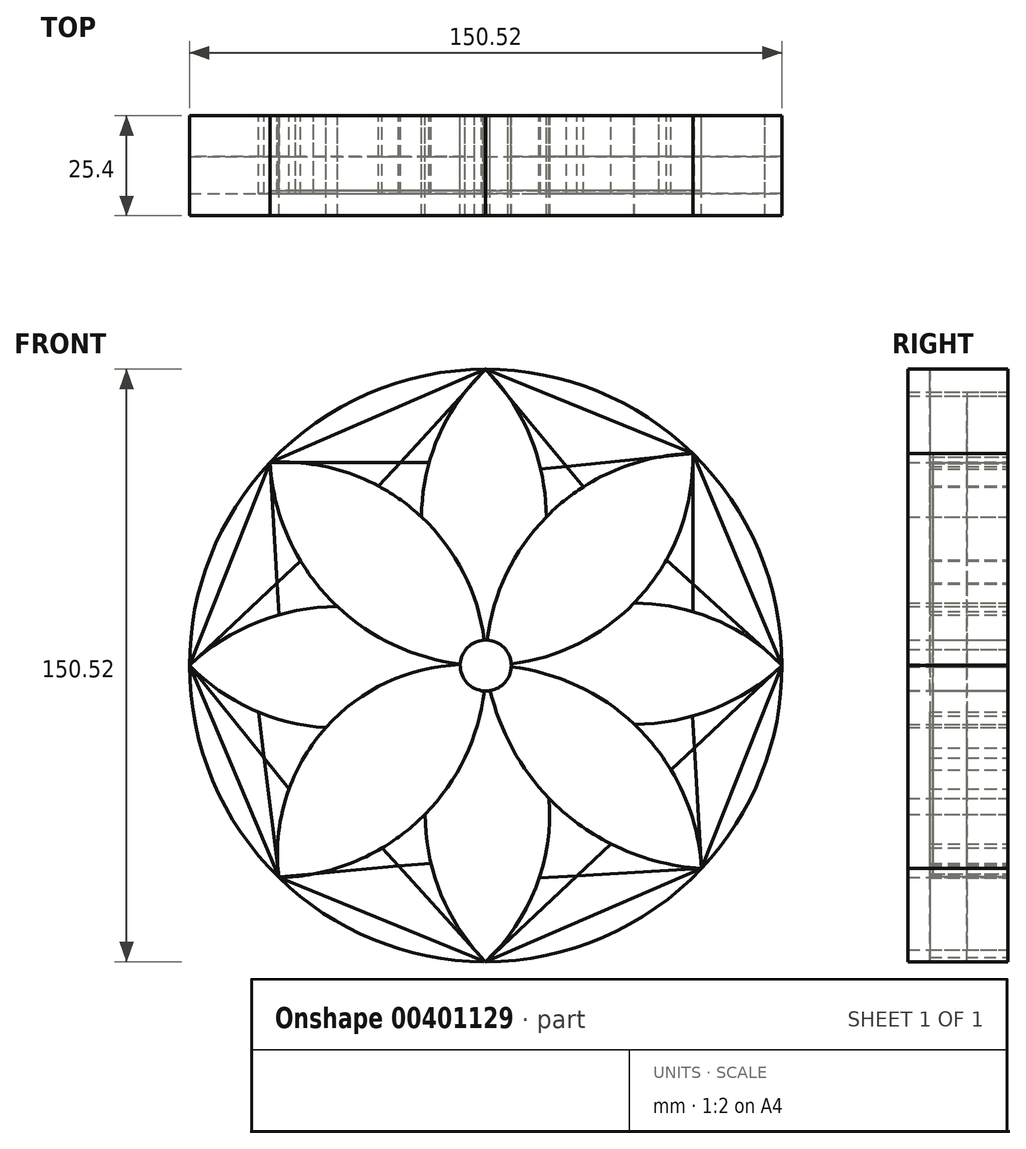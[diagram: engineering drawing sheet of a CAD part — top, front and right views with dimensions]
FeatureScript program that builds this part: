
annotation { "Feature Type Name" : "Feature", "Feature Type Description" : "" }
export const myFeature = defineFeature(function(context is Context, id is Id, definition is map)
    precondition{}
    {
        {
            var Q0;
            Q0=qCreatedBy(makeId("Front.planeOp"),FACE);
            var sketch = newSketch(context, id + "F0", { "sketchPlane" : qUnion([Q0])});
            skCircle(sketch, "E0", {"center": v(0, 0) * mm, "radius": 75.26 * mm});
            skCircle(sketch, "E1", {"center": v(0, 0) * mm, "radius": 6.49 * mm});
            skArc(sketch, "E2", {"start": v(0, 75.26) * mm, "mid": v(-12.03, 58.18) * mm, "end": v(-16.3, 37.72) * mm});
            skArc(sketch, "E3", {"start": v(15.38, 37.73) * mm, "mid": v(11.37, 58) * mm, "end": v(0, 75.26) * mm});
            skArc(sketch, "E4", {"start": v(75.26, 0) * mm, "mid": v(58.07, 11.72) * mm, "end": v(37.68, 15.86) * mm});
            skArc(sketch, "E5", {"start": v(37.72, -14.94) * mm, "mid": v(57.92, -11.05) * mm, "end": v(75.26, 0) * mm});
            skArc(sketch, "E6", {"start": v(-0.06, -75.26) * mm, "mid": v(12.73, -56.35) * mm, "end": v(16.12, -33.78) * mm});
            skArc(sketch, "E7", {"start": v(-15.42, -37.83) * mm, "mid": v(-15.03, -44.13) * mm, "end": v(-13.9, -50.35) * mm});
            skArc(sketch, "E8", {"start": v(-75.26, 0) * mm, "mid": v(-59.41, -11.13) * mm, "end": v(-40.6, -15.77) * mm});
            skArc(sketch, "E9", {"start": v(52.61, 53.82) * mm, "mid": v(17.65, 39.9) * mm, "end": v(0.38, 6.47) * mm});
            skArc(sketch, "E10", {"start": v(54.83, -51.55) * mm, "mid": v(39.96, -17.17) * mm, "end": v(6.47, -0.37) * mm});
            skArc(sketch, "E11", {"start": v(1.14, -6.38) * mm, "mid": v(20.5, -37.86) * mm, "end": v(54.83, -51.55) * mm});
            skArc(sketch, "E12", {"start": v(-52.56, -53.87) * mm, "mid": v(-17.6, -39.93) * mm, "end": v(-0.37, -6.47) * mm});
            skArc(sketch, "E13", {"start": v(-6.48, 0.2) * mm, "mid": v(-41.42, -16.7) * mm, "end": v(-52.56, -53.87) * mm});
            skArc(sketch, "E14", {"start": v(-54.83, 51.55) * mm, "mid": v(-39.94, 17.2) * mm, "end": v(-6.47, 0.38) * mm});
            skLineSegment(sketch, "E15", {"start": v(-0.1, 0.1) * mm, "end": v(-0.1, 0.1) * mm});
            skLineSegment(sketch, "E16.trimOffspring", {"start": v(0, 0) * mm, "end": v(0, 0) * mm});
            skArc(sketch, "E17.trimOffspring", {"start": v(6.47, 0.4) * mm, "mid": v(39.84, 18.21) * mm, "end": v(52.61, 53.82) * mm});
            skArc(sketch, "E18.trimOffspring", {"start": v(-37.68, 14.94) * mm, "mid": v(-57.9, 11.06) * mm, "end": v(-75.26, 0) * mm});
            skArc(sketch, "E19.trimOffspring", {"start": v(-0.4, 6.47) * mm, "mid": v(-18.67, 39.81) * mm, "end": v(-54.83, 51.55) * mm});
            skLineSegment(sketch, "E20", {"start": v(-75.26, 0) * mm, "end": v(-54.83, 51.55) * mm});
            skLineSegment(sketch, "E21", {"start": v(-54.83, 51.55) * mm, "end": v(-52.47, 12.9) * mm});
            skLineSegment(sketch, "E22", {"start": v(-75.26, 0) * mm, "end": v(-47.06, 26.58) * mm});
            skLineSegment(sketch, "E23", {"start": v(52.61, 53.82) * mm, "end": v(75.26, 0) * mm});
            skLineSegment(sketch, "E24", {"start": v(75.26, 0) * mm, "end": v(45.9, 26.86) * mm});
            skPoint(sketch, "E25.endSnap0", {"position": v(49.26, 40.34) * mm});
            skPoint(sketch, "E25.end.orphan", {"position": v(49.26, 14.55) * mm});
            skLineSegment(sketch, "E26", {"start": v(52.61, 53.82) * mm, "end": v(52.61, 13.68) * mm});
            skLineSegment(sketch, "E27", {"start": v(-75.26, 0) * mm, "end": v(-52.56, -53.87) * mm});
            skLineSegment(sketch, "E28", {"start": v(-52.56, -53.87) * mm, "end": v(-57.77, -11.84) * mm});
            skLineSegment(sketch, "E29", {"start": v(-75.26, 0) * mm, "end": v(-49.97, -31.35) * mm});
            skLineSegment(sketch, "E30", {"start": v(75.26, 0) * mm, "end": v(54.83, -51.55) * mm});
            skLineSegment(sketch, "E31", {"start": v(54.83, -51.55) * mm, "end": v(52.52, -12.88) * mm});
            skLineSegment(sketch, "E32", {"start": v(75.26, 0) * mm, "end": v(47.08, -26.56) * mm});
            skLineSegment(sketch, "E33", {"start": v(-54.83, 51.55) * mm, "end": v(0, 75.26) * mm});
            skLineSegment(sketch, "E34", {"start": v(0, 75.26) * mm, "end": v(-27.21, 45.55) * mm});
            skLineSegment(sketch, "E35", {"start": v(-54.83, 51.55) * mm, "end": v(-14.39, 51.55) * mm});
            skLineSegment(sketch, "E36", {"start": v(0, 75.26) * mm, "end": v(52.61, 53.82) * mm});
            skLineSegment(sketch, "E37", {"start": v(52.61, 53.82) * mm, "end": v(13.97, 49.86) * mm});
            skLineSegment(sketch, "E38", {"start": v(0, 75.26) * mm, "end": v(24.84, 45.4) * mm});
            skLineSegment(sketch, "E39", {"start": v(-52.56, -53.87) * mm, "end": v(-0.06, -75.26) * mm});
            skLineSegment(sketch, "E40", {"start": v(-52.57, -53.76) * mm, "end": v(-52.59, -53.77) * mm});
            skLineSegment(sketch, "E41", {"start": v(-52.59, -53.77) * mm, "end": v(-13.97, -50.22) * mm});
            skLineSegment(sketch, "E42", {"start": v(-13.97, -50.22) * mm, "end": v(-13.9, -50.35) * mm});
            skArc(sketch, "E43.trimOffspring", {"start": v(-1.12, -74.14) * mm, "mid": v(-0.6, -74.7) * mm, "end": v(-0.06, -75.26) * mm});
            skLineSegment(sketch, "E44", {"start": v(-26.3, -46.36) * mm, "end": v(-0.06, -75.26) * mm});
            skLineSegment(sketch, "E45", {"start": v(-0.06, -75.26) * mm, "end": v(54.83, -51.55) * mm});
            skLineSegment(sketch, "E46", {"start": v(54.83, -51.55) * mm, "end": v(13.58, -54.02) * mm});
            skLineSegment(sketch, "E47", {"start": v(-0.2, -75.11) * mm, "end": v(-0.42, -75.46) * mm});
            skLineSegment(sketch, "E48", {"start": v(-0.06, -75.26) * mm, "end": v(31.85, -45.35) * mm});
            skArc(sketch, "E49", {"start": v(-15.42, -37.83) * mm, "mid": v(-11.4, -58.05) * mm, "end": v(-0.06, -75.26) * mm});
            skLineSegment(sketch, "E50.trimOffspring", {"start": v(-1.2, -74) * mm, "end": v(-0.42, -75.46) * mm});
            skSolve(sketch);
        }
        {
            var Q0;
            {var subQ0=sQuery(id+"F0.wireOp",EDGE,"E20");Q0=makeQuery(id+"F0.imprint","IMPRINT",FACE,{"disambiguationData":[TD([[makeQuery(id+"F0.imprint","IMPRINT",EDGE,{"derivedFrom":subQ0}),1.0]])]});}
            var Q1;
            {var subQ0=sQuery(id+"F0.wireOp",EDGE,"E33");Q1=makeQuery(id+"F0.imprint","IMPRINT",FACE,{"disambiguationData":[TD([[makeQuery(id+"F0.imprint","IMPRINT",EDGE,{"derivedFrom":subQ0}),1.0]])]});}
            var Q2;
            {var subQ0=sQuery(id+"F0.wireOp",EDGE,"E36");Q2=makeQuery(id+"F0.imprint","IMPRINT",FACE,{"disambiguationData":[TD([[makeQuery(id+"F0.imprint","IMPRINT",EDGE,{"derivedFrom":subQ0}),1.0]])]});}
            var Q3;
            {var subQ0=sQuery(id+"F0.wireOp",EDGE,"E23");Q3=makeQuery(id+"F0.imprint","IMPRINT",FACE,{"disambiguationData":[TD([[makeQuery(id+"F0.imprint","IMPRINT",EDGE,{"derivedFrom":subQ0}),1.0]])]});}
            var Q4;
            {var subQ0=sQuery(id+"F0.wireOp",EDGE,"E30");Q4=makeQuery(id+"F0.imprint","IMPRINT",FACE,{"disambiguationData":[TD([[makeQuery(id+"F0.imprint","IMPRINT",EDGE,{"derivedFrom":subQ0}),1.0]])]});}
            var Q5;
            {var subQ0=sQuery(id+"F0.wireOp",EDGE,"E45");Q5=makeQuery(id+"F0.imprint","IMPRINT",FACE,{"disambiguationData":[TD([[makeQuery(id+"F0.imprint","IMPRINT",EDGE,{"derivedFrom":subQ0}),-1.0]])]});}
            var Q6;
            {var subQ1=sQuery(id+"F0.wireOp",EDGE,"E0");var subQ3=sQuery(id+"F0.wireOp",EDGE,"E50.trimOffspring");var subQ4=makeQuery(id+"F0.imprint","INTERSECT",VERTEX,{"derivedFrom":[subQ1,subQ3]});Q6=makeQuery(id+"F0.imprint","IMPRINT",FACE,{"disambiguationData":[TD([[makeQuery(id+"F0.imprint","IMPRINT",EDGE,{"disambiguationData":[TD([[subQ4,1.0]])],"derivedFrom":subQ3}),-1.0]])]});}
            var Q7;
            {var subQ0=sQuery(id+"F0.wireOp",EDGE,"E27");Q7=makeQuery(id+"F0.imprint","IMPRINT",FACE,{"disambiguationData":[TD([[makeQuery(id+"F0.imprint","IMPRINT",EDGE,{"derivedFrom":subQ0}),-1.0]])]});}
            var Q8;
            {var subQ0=sQuery(id+"F0.wireOp",EDGE,"E13");var subQ3=sQuery(id+"F0.wireOp",EDGE,"E1");var subQ4=makeQuery(id+"F0.imprint","INTERSECT",VERTEX,{"derivedFrom":[subQ3,subQ0]});Q8=makeQuery(id+"F0.imprint","IMPRINT",FACE,{"disambiguationData":[TD([[makeQuery(id+"F0.imprint","IMPRINT",EDGE,{"disambiguationData":[TD([[subQ4,1.0]])],"derivedFrom":subQ3}),-1.0]])]});}
            var Q9;
            {var subQ8=sQuery(id+"F0.wireOp",EDGE,"E10");var subQ11=sQuery(id+"F0.wireOp",EDGE,"E1");var subQ12=makeQuery(id+"F0.imprint","INTERSECT",VERTEX,{"derivedFrom":[subQ11,subQ8]});Q9=makeQuery(id+"F0.imprint","IMPRINT",FACE,{"disambiguationData":[TD([[makeQuery(id+"F0.imprint","IMPRINT",EDGE,{"disambiguationData":[TD([[subQ12,-1.0]])],"derivedFrom":subQ11}),-1.0]])]});}
            var Q10;
            {var subQ6=sQuery(id+"F0.wireOp",EDGE,"E9");var subQ10=sQuery(id+"F0.wireOp",EDGE,"E1");var subQ11=makeQuery(id+"F0.imprint","INTERSECT",VERTEX,{"derivedFrom":[subQ10,subQ6]});Q10=makeQuery(id+"F0.imprint","IMPRINT",FACE,{"disambiguationData":[TD([[makeQuery(id+"F0.imprint","IMPRINT",EDGE,{"disambiguationData":[TD([[subQ11,-1.0]])],"derivedFrom":subQ10}),-1.0]])]});}
            var Q11;
            {var subQ5=sQuery(id+"F0.wireOp",EDGE,"E11");var subQ7=sQuery(id+"F0.wireOp",EDGE,"E1");var subQ8=makeQuery(id+"F0.imprint","INTERSECT",VERTEX,{"derivedFrom":[subQ7,subQ5]});Q11=makeQuery(id+"F0.imprint","IMPRINT",FACE,{"disambiguationData":[TD([[makeQuery(id+"F0.imprint","IMPRINT",EDGE,{"disambiguationData":[TD([[subQ8,1.0]])],"derivedFrom":subQ7}),-1.0]])]});}
            extrude(context, id + "F1", {"entities" : qUnion([Q0, Q1, Q2, Q3, Q4, Q5, Q6, Q7, Q8, Q9, Q10, Q11]), "depth" : 25.4 * mm});
        }
        {
            var Q0;
            {var subQ0=sQuery(id+"F0.wireOp",EDGE,"E9");var subQ2=sQuery(id+"F0.wireOp",EDGE,"E1");var subQ3=makeQuery(id+"F0.imprint","INTERSECT",VERTEX,{"derivedFrom":[subQ2,subQ0]});Q0=makeQuery(id+"F0.imprint","IMPRINT",FACE,{"disambiguationData":[TD([[makeQuery(id+"F0.imprint","IMPRINT",EDGE,{"disambiguationData":[TD([[subQ3,1.0]])],"derivedFrom":subQ2}),-1.0]])]});}
            var Q1;
            {var subQ0=sQuery(id+"F0.wireOp",EDGE,"E10");var subQ2=sQuery(id+"F0.wireOp",EDGE,"E1");var subQ3=makeQuery(id+"F0.imprint","INTERSECT",VERTEX,{"derivedFrom":[subQ2,subQ0]});Q1=makeQuery(id+"F0.imprint","IMPRINT",FACE,{"disambiguationData":[TD([[makeQuery(id+"F0.imprint","IMPRINT",EDGE,{"disambiguationData":[TD([[subQ3,1.0]])],"derivedFrom":subQ2}),-1.0]])]});}
            var Q2;
            {var subQ0=sQuery(id+"F0.wireOp",EDGE,"E12");var subQ1=sQuery(id+"F0.wireOp",EDGE,"E1");var subQ2=makeQuery(id+"F0.imprint","INTERSECT",VERTEX,{"derivedFrom":[subQ1,subQ0]});Q2=makeQuery(id+"F0.imprint","IMPRINT",FACE,{"disambiguationData":[TD([[makeQuery(id+"F0.imprint","IMPRINT",EDGE,{"disambiguationData":[TD([[subQ2,1.0]])],"derivedFrom":subQ1}),-1.0]])]});}
            var Q3;
            {var subQ0=sQuery(id+"F0.wireOp",EDGE,"E14");var subQ1=sQuery(id+"F0.wireOp",EDGE,"E1");var subQ2=makeQuery(id+"F0.imprint","INTERSECT",VERTEX,{"derivedFrom":[subQ1,subQ0]});Q3=makeQuery(id+"F0.imprint","IMPRINT",FACE,{"disambiguationData":[TD([[makeQuery(id+"F0.imprint","IMPRINT",EDGE,{"disambiguationData":[TD([[subQ2,1.0]])],"derivedFrom":subQ1}),-1.0]])]});}
            extrude(context, id + "F2", {"entities" : qUnion([Q0, Q1, Q2, Q3]), "depth" : 19.05 * mm});
        }
        {
            var Q0;
            {var subQ0=sQuery(id+"F0.wireOp",EDGE,"E1");var subQ4=makeQuery(id+"F0.imprint","INTERSECT",VERTEX,{"derivedFrom":[subQ0,sQuery(id+"F0.wireOp",EDGE,"E9")]});Q0=makeQuery(id+"F0.imprint","IMPRINT",FACE,{"disambiguationData":[TD([[makeQuery(id+"F0.imprint","IMPRINT",EDGE,{"disambiguationData":[TD([[subQ4,1.0]])],"derivedFrom":subQ0}),1.0]])]});}
            var Q1;
            {var subQ0=sQuery(id+"F0.wireOp",EDGE,"E20");Q1=makeQuery(id+"F0.imprint","IMPRINT",FACE,{"disambiguationData":[TD([[makeQuery(id+"F0.imprint","IMPRINT",EDGE,{"derivedFrom":subQ0}),-1.0]])]});}
            var Q2;
            {var subQ5=sQuery(id+"F0.wireOp",EDGE,"E33");Q2=makeQuery(id+"F0.imprint","IMPRINT",FACE,{"disambiguationData":[TD([[makeQuery(id+"F0.imprint","IMPRINT",EDGE,{"derivedFrom":subQ5}),-1.0]])]});}
            var Q3;
            {var subQ5=sQuery(id+"F0.wireOp",EDGE,"E36");Q3=makeQuery(id+"F0.imprint","IMPRINT",FACE,{"disambiguationData":[TD([[makeQuery(id+"F0.imprint","IMPRINT",EDGE,{"derivedFrom":subQ5}),-1.0]])]});}
            var Q4;
            {var subQ5=sQuery(id+"F0.wireOp",EDGE,"E23");Q4=makeQuery(id+"F0.imprint","IMPRINT",FACE,{"disambiguationData":[TD([[makeQuery(id+"F0.imprint","IMPRINT",EDGE,{"derivedFrom":subQ5}),-1.0]])]});}
            var Q5;
            {var subQ0=sQuery(id+"F0.wireOp",EDGE,"E30");Q5=makeQuery(id+"F0.imprint","IMPRINT",FACE,{"disambiguationData":[TD([[makeQuery(id+"F0.imprint","IMPRINT",EDGE,{"derivedFrom":subQ0}),-1.0]])]});}
            var Q6;
            {var subQ0=sQuery(id+"F0.wireOp",EDGE,"E45");Q6=makeQuery(id+"F0.imprint","IMPRINT",FACE,{"disambiguationData":[TD([[makeQuery(id+"F0.imprint","IMPRINT",EDGE,{"derivedFrom":subQ0}),1.0]])]});}
            var Q7;
            {var subQ0=sQuery(id+"F0.wireOp",EDGE,"E41");var subQ1=sQuery(id+"F0.wireOp",EDGE,"E12");var subQ2=makeQuery(id+"F0.imprint","INTERSECT",VERTEX,{"derivedFrom":[subQ1,subQ0]});Q7=makeQuery(id+"F0.imprint","IMPRINT",FACE,{"disambiguationData":[TD([[makeQuery(id+"F0.imprint","IMPRINT",EDGE,{"disambiguationData":[TD([[subQ2,-1.0]])],"derivedFrom":subQ0}),-1.0]])]});}
            var Q8;
            {var subQ4=sQuery(id+"F0.wireOp",EDGE,"E27");Q8=makeQuery(id+"F0.imprint","IMPRINT",FACE,{"disambiguationData":[TD([[makeQuery(id+"F0.imprint","IMPRINT",EDGE,{"derivedFrom":subQ4}),1.0]])]});}
            var Q9;
            {var subQ0=sQuery(id+"F0.wireOp",EDGE,"E13");var subQ1=sQuery(id+"F0.wireOp",EDGE,"E8");var subQ2=makeQuery(id+"F0.imprint","INTERSECT",VERTEX,{"derivedFrom":[subQ1,subQ0]});Q9=makeQuery(id+"F0.imprint","IMPRINT",FACE,{"disambiguationData":[TD([[makeQuery(id+"F0.imprint","IMPRINT",EDGE,{"disambiguationData":[TD([[subQ2,1.0]])],"derivedFrom":subQ1}),-1.0]])]});}
            var Q10;
            {var subQ5=sQuery(id+"F0.wireOp",EDGE,"E42");Q10=makeQuery(id+"F0.imprint","IMPRINT",FACE,{"disambiguationData":[TD([[makeQuery(id+"F0.imprint","IMPRINT",EDGE,{"derivedFrom":subQ5}),1.0]])]});}
            var Q11;
            {var subQ0=sQuery(id+"F0.wireOp",EDGE,"E11");var subQ1=sQuery(id+"F0.wireOp",EDGE,"E6");var subQ2=makeQuery(id+"F0.imprint","INTERSECT",VERTEX,{"derivedFrom":[subQ1,subQ0]});Q11=makeQuery(id+"F0.imprint","IMPRINT",FACE,{"disambiguationData":[TD([[makeQuery(id+"F0.imprint","IMPRINT",EDGE,{"disambiguationData":[TD([[subQ2,1.0]])],"derivedFrom":subQ1}),-1.0]])]});}
            var Q12;
            {var subQ0=sQuery(id+"F0.wireOp",EDGE,"E10");var subQ1=sQuery(id+"F0.wireOp",EDGE,"E5");var subQ2=makeQuery(id+"F0.imprint","INTERSECT",VERTEX,{"derivedFrom":[subQ1,subQ0]});Q12=makeQuery(id+"F0.imprint","IMPRINT",FACE,{"disambiguationData":[TD([[makeQuery(id+"F0.imprint","IMPRINT",EDGE,{"disambiguationData":[TD([[subQ2,-1.0]])],"derivedFrom":subQ1}),-1.0]])]});}
            var Q13;
            {var subQ0=sQuery(id+"F0.wireOp",EDGE,"E17.trimOffspring");var subQ1=sQuery(id+"F0.wireOp",EDGE,"E4");var subQ2=makeQuery(id+"F0.imprint","INTERSECT",VERTEX,{"derivedFrom":[subQ1,subQ0]});Q13=makeQuery(id+"F0.imprint","IMPRINT",FACE,{"disambiguationData":[TD([[makeQuery(id+"F0.imprint","IMPRINT",EDGE,{"disambiguationData":[TD([[subQ2,1.0]])],"derivedFrom":subQ1}),-1.0]])]});}
            var Q14;
            {var subQ0=sQuery(id+"F0.wireOp",EDGE,"E9");var subQ1=sQuery(id+"F0.wireOp",EDGE,"E3");var subQ2=makeQuery(id+"F0.imprint","INTERSECT",VERTEX,{"derivedFrom":[subQ1,subQ0]});Q14=makeQuery(id+"F0.imprint","IMPRINT",FACE,{"disambiguationData":[TD([[makeQuery(id+"F0.imprint","IMPRINT",EDGE,{"disambiguationData":[TD([[subQ2,-1.0]])],"derivedFrom":subQ1}),-1.0]])]});}
            var Q15;
            {var subQ0=sQuery(id+"F0.wireOp",EDGE,"E19.trimOffspring");var subQ1=sQuery(id+"F0.wireOp",EDGE,"E2");var subQ2=makeQuery(id+"F0.imprint","INTERSECT",VERTEX,{"derivedFrom":[subQ1,subQ0]});Q15=makeQuery(id+"F0.imprint","IMPRINT",FACE,{"disambiguationData":[TD([[makeQuery(id+"F0.imprint","IMPRINT",EDGE,{"disambiguationData":[TD([[subQ2,1.0]])],"derivedFrom":subQ1}),-1.0]])]});}
            var Q16;
            {var subQ0=sQuery(id+"F0.wireOp",EDGE,"E18.trimOffspring");var subQ1=sQuery(id+"F0.wireOp",EDGE,"E14");var subQ2=makeQuery(id+"F0.imprint","INTERSECT",VERTEX,{"derivedFrom":[subQ1,subQ0]});Q16=makeQuery(id+"F0.imprint","IMPRINT",FACE,{"disambiguationData":[TD([[makeQuery(id+"F0.imprint","IMPRINT",EDGE,{"disambiguationData":[TD([[subQ2,1.0]])],"derivedFrom":subQ1}),-1.0]])]});}
            extrude(context, id + "F3", {"entities" : qUnion([Q0, Q1, Q2, Q3, Q4, Q5, Q6, Q7, Q8, Q9, Q10, Q11, Q12, Q13, Q14, Q15, Q16]), "depth" : 19.8 * mm});
        }
        {
            var Q0;
            {var subQ0=sQuery(id+"F0.wireOp",EDGE,"E37");var subQ1=sQuery(id+"F0.wireOp",EDGE,"E3");var subQ2=makeQuery(id+"F0.imprint","INTERSECT",VERTEX,{"derivedFrom":[subQ1,subQ0]});Q0=makeQuery(id+"F0.imprint","IMPRINT",FACE,{"disambiguationData":[TD([[makeQuery(id+"F0.imprint","IMPRINT",EDGE,{"disambiguationData":[TD([[subQ2,-1.0]])],"derivedFrom":subQ1}),-1.0]])]});}
            var Q1;
            {var subQ0=sQuery(id+"F0.wireOp",EDGE,"E38");var subQ1=sQuery(id+"F0.wireOp",EDGE,"E9");var subQ2=makeQuery(id+"F0.imprint","INTERSECT",VERTEX,{"derivedFrom":[subQ1,subQ0]});Q1=makeQuery(id+"F0.imprint","IMPRINT",FACE,{"disambiguationData":[TD([[makeQuery(id+"F0.imprint","IMPRINT",EDGE,{"disambiguationData":[TD([[subQ2,1.0]])],"derivedFrom":subQ1}),-1.0]])]});}
            var Q2;
            {var subQ0=sQuery(id+"F0.wireOp",EDGE,"E24");var subQ1=sQuery(id+"F0.wireOp",EDGE,"E17.trimOffspring");var subQ2=makeQuery(id+"F0.imprint","INTERSECT",VERTEX,{"derivedFrom":[subQ1,subQ0]});Q2=makeQuery(id+"F0.imprint","IMPRINT",FACE,{"disambiguationData":[TD([[makeQuery(id+"F0.imprint","IMPRINT",EDGE,{"disambiguationData":[TD([[subQ2,-1.0]])],"derivedFrom":subQ1}),-1.0]])]});}
            var Q3;
            {var subQ0=sQuery(id+"F0.wireOp",EDGE,"E26");var subQ1=sQuery(id+"F0.wireOp",EDGE,"E4");var subQ2=makeQuery(id+"F0.imprint","INTERSECT",VERTEX,{"derivedFrom":[subQ1,subQ0]});Q3=makeQuery(id+"F0.imprint","IMPRINT",FACE,{"disambiguationData":[TD([[makeQuery(id+"F0.imprint","IMPRINT",EDGE,{"disambiguationData":[TD([[subQ2,1.0]])],"derivedFrom":subQ1}),-1.0]])]});}
            var Q4;
            {var subQ1=sQuery(id+"F0.wireOp",EDGE,"E5");var subQ3=sQuery(id+"F0.wireOp",EDGE,"E31");var subQ4=makeQuery(id+"F0.imprint","INTERSECT",VERTEX,{"derivedFrom":[subQ1,subQ3]});Q4=makeQuery(id+"F0.imprint","IMPRINT",FACE,{"disambiguationData":[TD([[makeQuery(id+"F0.imprint","IMPRINT",EDGE,{"disambiguationData":[TD([[subQ4,1.0]])],"derivedFrom":subQ3}),-1.0]])]});}
            var Q5;
            {var subQ1=sQuery(id+"F0.wireOp",EDGE,"E10");var subQ3=sQuery(id+"F0.wireOp",EDGE,"E32");var subQ4=makeQuery(id+"F0.imprint","INTERSECT",VERTEX,{"derivedFrom":[subQ1,subQ3]});Q5=makeQuery(id+"F0.imprint","IMPRINT",FACE,{"disambiguationData":[TD([[makeQuery(id+"F0.imprint","IMPRINT",EDGE,{"disambiguationData":[TD([[subQ4,1.0]])],"derivedFrom":subQ3}),1.0]])]});}
            var Q6;
            {var subQ1=sQuery(id+"F0.wireOp",EDGE,"E11");var subQ3=sQuery(id+"F0.wireOp",EDGE,"E48");var subQ4=makeQuery(id+"F0.imprint","INTERSECT",VERTEX,{"derivedFrom":[subQ1,subQ3]});Q6=makeQuery(id+"F0.imprint","IMPRINT",FACE,{"disambiguationData":[TD([[makeQuery(id+"F0.imprint","IMPRINT",EDGE,{"disambiguationData":[TD([[subQ4,1.0]])],"derivedFrom":subQ3}),-1.0]])]});}
            var Q7;
            {var subQ1=sQuery(id+"F0.wireOp",EDGE,"E6");var subQ3=sQuery(id+"F0.wireOp",EDGE,"E46");var subQ4=makeQuery(id+"F0.imprint","INTERSECT",VERTEX,{"derivedFrom":[subQ1,subQ3]});Q7=makeQuery(id+"F0.imprint","IMPRINT",FACE,{"disambiguationData":[TD([[makeQuery(id+"F0.imprint","IMPRINT",EDGE,{"disambiguationData":[TD([[subQ4,1.0]])],"derivedFrom":subQ3}),1.0]])]});}
            var Q8;
            {var subQ0=sQuery(id+"F0.wireOp",EDGE,"E42");Q8=makeQuery(id+"F0.imprint","IMPRINT",FACE,{"disambiguationData":[TD([[makeQuery(id+"F0.imprint","IMPRINT",EDGE,{"derivedFrom":subQ0}),-1.0]])]});}
            var Q9;
            {var subQ0=sQuery(id+"F0.wireOp",EDGE,"E44");var subQ1=sQuery(id+"F0.wireOp",EDGE,"E12");var subQ2=makeQuery(id+"F0.imprint","INTERSECT",VERTEX,{"derivedFrom":[subQ1,subQ0]});Q9=makeQuery(id+"F0.imprint","IMPRINT",FACE,{"disambiguationData":[TD([[makeQuery(id+"F0.imprint","IMPRINT",EDGE,{"disambiguationData":[TD([[subQ2,1.0]])],"derivedFrom":subQ1}),-1.0]])]});}
            var Q10;
            {var subQ0=sQuery(id+"F0.wireOp",EDGE,"E29");var subQ1=sQuery(id+"F0.wireOp",EDGE,"E13");var subQ2=makeQuery(id+"F0.imprint","INTERSECT",VERTEX,{"derivedFrom":[subQ1,subQ0]});Q10=makeQuery(id+"F0.imprint","IMPRINT",FACE,{"disambiguationData":[TD([[makeQuery(id+"F0.imprint","IMPRINT",EDGE,{"disambiguationData":[TD([[subQ2,-1.0]])],"derivedFrom":subQ1}),-1.0]])]});}
            var Q11;
            {var subQ1=sQuery(id+"F0.wireOp",EDGE,"E8");var subQ3=sQuery(id+"F0.wireOp",EDGE,"E28");var subQ4=makeQuery(id+"F0.imprint","INTERSECT",VERTEX,{"derivedFrom":[subQ1,subQ3]});Q11=makeQuery(id+"F0.imprint","IMPRINT",FACE,{"disambiguationData":[TD([[makeQuery(id+"F0.imprint","IMPRINT",EDGE,{"disambiguationData":[TD([[subQ4,1.0]])],"derivedFrom":subQ3}),1.0]])]});}
            var Q12;
            {var subQ1=sQuery(id+"F0.wireOp",EDGE,"E18.trimOffspring");var subQ3=sQuery(id+"F0.wireOp",EDGE,"E21");var subQ4=makeQuery(id+"F0.imprint","INTERSECT",VERTEX,{"derivedFrom":[subQ1,subQ3]});Q12=makeQuery(id+"F0.imprint","IMPRINT",FACE,{"disambiguationData":[TD([[makeQuery(id+"F0.imprint","IMPRINT",EDGE,{"disambiguationData":[TD([[subQ4,1.0]])],"derivedFrom":subQ3}),-1.0]])]});}
            var Q13;
            {var subQ1=sQuery(id+"F0.wireOp",EDGE,"E14");var subQ3=sQuery(id+"F0.wireOp",EDGE,"E22");var subQ4=makeQuery(id+"F0.imprint","INTERSECT",VERTEX,{"derivedFrom":[subQ1,subQ3]});Q13=makeQuery(id+"F0.imprint","IMPRINT",FACE,{"disambiguationData":[TD([[makeQuery(id+"F0.imprint","IMPRINT",EDGE,{"disambiguationData":[TD([[subQ4,1.0]])],"derivedFrom":subQ3}),1.0]])]});}
            var Q14;
            {var subQ0=sQuery(id+"F0.wireOp",EDGE,"E34");var subQ1=sQuery(id+"F0.wireOp",EDGE,"E19.trimOffspring");var subQ2=makeQuery(id+"F0.imprint","INTERSECT",VERTEX,{"derivedFrom":[subQ1,subQ0]});Q14=makeQuery(id+"F0.imprint","IMPRINT",FACE,{"disambiguationData":[TD([[makeQuery(id+"F0.imprint","IMPRINT",EDGE,{"disambiguationData":[TD([[subQ2,-1.0]])],"derivedFrom":subQ1}),-1.0]])]});}
            var Q15;
            {var subQ0=sQuery(id+"F0.wireOp",EDGE,"E35");var subQ1=sQuery(id+"F0.wireOp",EDGE,"E2");var subQ2=makeQuery(id+"F0.imprint","INTERSECT",VERTEX,{"derivedFrom":[subQ1,subQ0]});Q15=makeQuery(id+"F0.imprint","IMPRINT",FACE,{"disambiguationData":[TD([[makeQuery(id+"F0.imprint","IMPRINT",EDGE,{"disambiguationData":[TD([[subQ2,1.0]])],"derivedFrom":subQ1}),-1.0]])]});}
            extrude(context, id + "F4", {"entities" : qUnion([Q0, Q1, Q2, Q3, Q4, Q5, Q6, Q7, Q8, Q9, Q10, Q11, Q12, Q13, Q14, Q15]), "depth" : 10.4 * mm});
        }
    });
